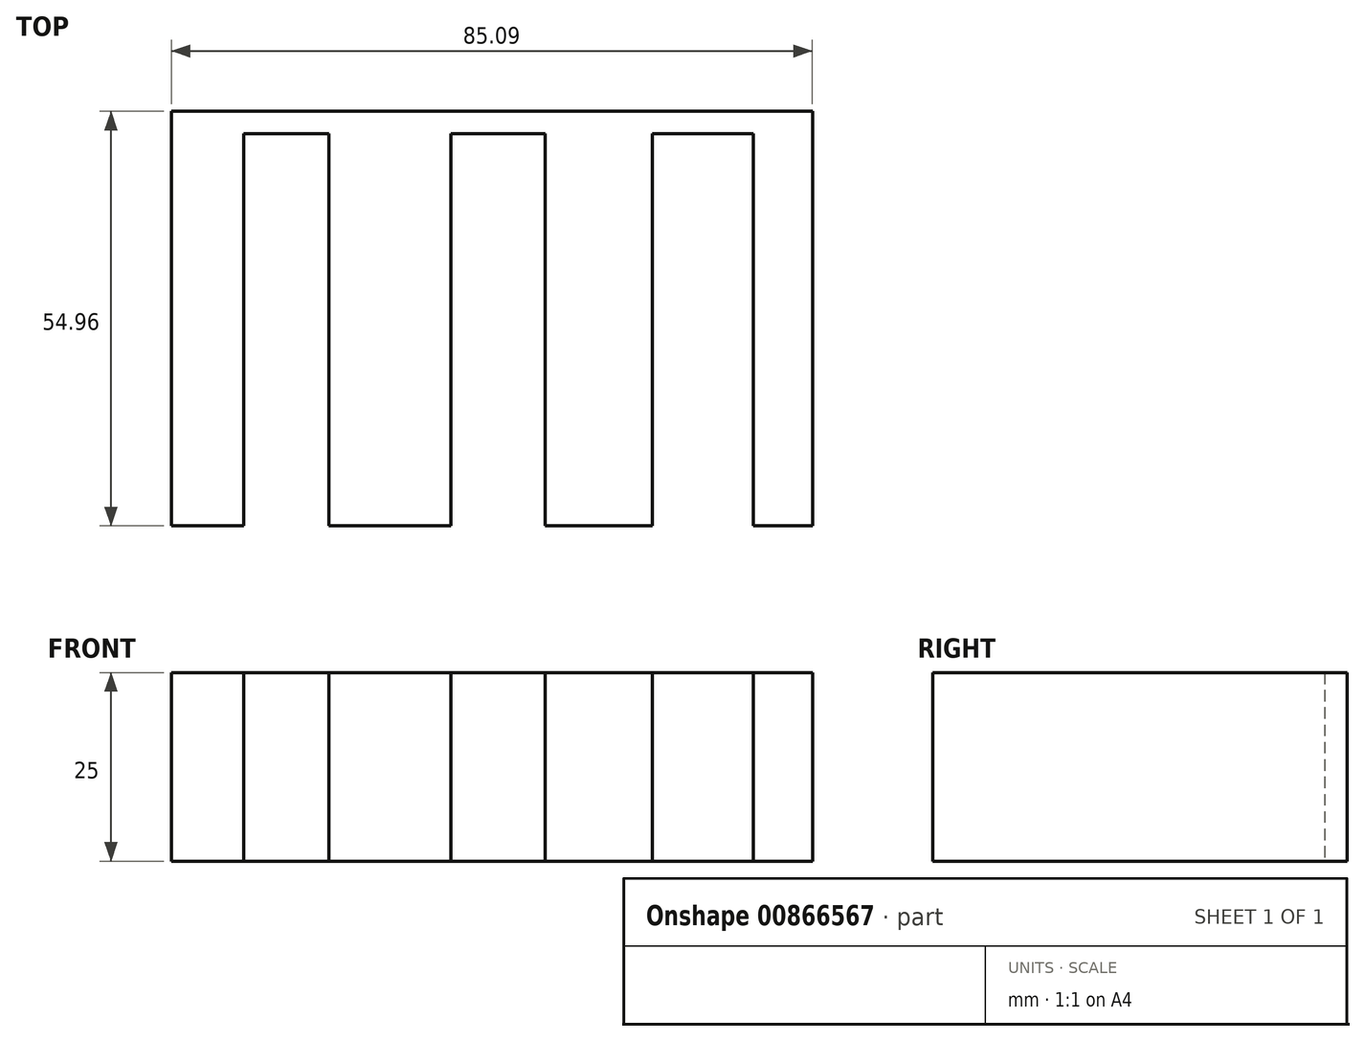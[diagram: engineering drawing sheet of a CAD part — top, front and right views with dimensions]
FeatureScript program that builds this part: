
annotation { "Feature Type Name" : "Feature", "Feature Type Description" : "" }
export const myFeature = defineFeature(function(context is Context, id is Id, definition is map)
    precondition{}
    {
        {
            var Q0;
            Q0=qCreatedBy(makeId("Top.planeOp"),FACE);
            var sketch = newSketch(context, id + "F0", { "sketchPlane" : qUnion([Q0])});
            skLineSegment(sketch, "E0", {"start": v(0, 0) * mm, "end": v(0, 51.97) * mm});
            skLineSegment(sketch, "E1", {"start": v(0, 51.97) * mm, "end": v(11.29, 51.97) * mm});
            skLineSegment(sketch, "E2", {"start": v(11.29, 51.97) * mm, "end": v(11.29, 0) * mm});
            skLineSegment(sketch, "E3", {"start": v(11.29, 0) * mm, "end": v(27.53, 0) * mm});
            skLineSegment(sketch, "E4", {"start": v(27.53, 0) * mm, "end": v(27.53, 51.97) * mm});
            skLineSegment(sketch, "E5", {"start": v(27.53, 51.97) * mm, "end": v(40.03, 51.97) * mm});
            skLineSegment(sketch, "E6", {"start": v(40.03, 51.97) * mm, "end": v(40.03, 0) * mm});
            skLineSegment(sketch, "E7", {"start": v(40.03, 0) * mm, "end": v(54.21, 0) * mm});
            skLineSegment(sketch, "E8", {"start": v(54.21, 0) * mm, "end": v(54.21, 51.97) * mm});
            skLineSegment(sketch, "E9", {"start": v(54.21, 51.97) * mm, "end": v(67.65, 51.97) * mm});
            skLineSegment(sketch, "E10", {"start": v(67.65, 51.97) * mm, "end": v(67.65, 0) * mm});
            skLineSegment(sketch, "E11", {"start": v(67.65, 0) * mm, "end": v(75.48, 0) * mm});
            skLineSegment(sketch, "E12", {"start": v(75.48, 0) * mm, "end": v(75.48, 54.96) * mm});
            skLineSegment(sketch, "E13", {"start": v(75.48, 54.96) * mm, "end": v(-9.61, 54.96) * mm});
            skLineSegment(sketch, "E14", {"start": v(-9.61, 54.96) * mm, "end": v(-9.61, 0) * mm});
            skLineSegment(sketch, "E15", {"start": v(-9.61, 0) * mm, "end": v(0, 0) * mm});
            skSolve(sketch);
        }
        {
            var Q0;
            Q0 = qSketchRegion(id + "F0", true);
            extrude(context, id + "F1", {"entities" : qUnion([Q0]), "depth" : 25 * mm, "offsetDistance" : 25 * mm});
        }
    });
